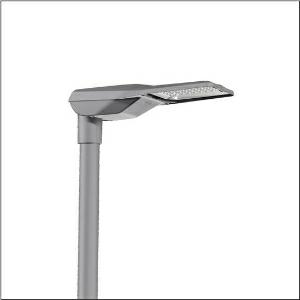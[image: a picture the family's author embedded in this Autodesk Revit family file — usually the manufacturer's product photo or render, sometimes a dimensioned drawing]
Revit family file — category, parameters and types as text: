
# Revit family: streetlight_sl_21_iq_mini___st1_5a_5xe2p31g08hb_126e
name_source: partatom
category: Lighting Fixtures
units: mm (PartAtom-declared; Revit-internal decimal feet)

## family parameters
Cut with Voids When Loaded = No
Host = Face
Light Source = No
Part Type = Normal
Room Calculation Point = No
Round Connector Dimension = Use Diameter
Shared = No

## types (1)
- --- (1 x LED, 9290 lm, 70.9 W, 3000K)
    Apparent Load = 71 VA
    CIE Flux Codes = 22 53 95 100 100
    Color Rendering = 70
    Color Temperature = 3000K
    Default Elevation = 1800 mm
    Description = Streetlight SL 21 iQ mini, mast luminaire, primary light control with lens, of PMMA, primary optical cover: cover, of toughened safety glass, transparent, light distribution: ST1.5a, light emission: direct distribution, primary light characteristic: asymmetric, installation type: post-top, side-entry, LED, High Power LED, rated luminous flux: 9.290lm, luminous efficacy: 131lm/W, light colour: 730, colour temperature: 3000K, control gear: iQ Street-Remote, control: Street-Remote, Auto-Match, Temp-Guard, Lumen-Switch, Night-Set, Smart-Wire, Light-Fading, Desk-Remote (wireless, voltage-free reading and setting of iQ features in the workshop via application-optimized NFC function/RFID function), optimised constant luminous flux control (CLO 2.0), pre-setting: linear dimming characteristic, mains connection: 220..240V, AC, 50/60Hz, start of lifetime: 71W, end of service life: 75W, reduction: 31W, luminaire housing, of diecast aluminium, powder-coated, Siteco® metallic grey (DB 702S), corrosivity category C5 mid according to DIN EN ISO 12944, please order mast flange separately, inclination adjustable: 0°, 5°, 10°, 15°, sealing non-destructively replaceable, multi-level sealing system, length: 628mm, width: 235mm, height: 110mm, mast flange for spigot size: 42mm (side-entry): 5XC10008XM4, 60/48mm (side-entry/post-top): 5XC10108XM2, 76/60mm (side-entry/post-top): 5XC10108XM1, mounting height: 4..8m, protection rating (complete): IP66, insulation class (complete): insulation class II (safety insulation), certification: CE, ENEC, ENEC+, VDE, impact resistance: IK10, permissible operating ambient temperature for outdoor applications: -40..+50°C, standard-compliant lighting for roads and squares, packaging unit: 1 piece

Light Distribution: ST1.5a
    Height = 110 mm
    Lamp = 1 x LED
    Lamp Light Flux = 9290 lm
    Lamp Power = 70.9 W
    Lamp count = 1
    Length = 625 mm
    Luminous efficacy = 131 lm/W
    Manufacturer = Siteco
    ModVariant = No
    Model = 5XE2P31G08HB
    Number of Poles = 1
    OnlyDefault = Yes
    Power Factor = 1
    Product Name = Streetlight SL 21 iQ mini | ST1.5a
    Product group = mast luminaire | pylon top
    ProductGroupID = 6100
    Protection Class = Protection class II
    Protection Degree = IP 66
    RLX_Detail_Level = 1
    RLX_Emergency_Light_Flux = 0 lm
    RLX_Emergency_Type = 0
    RLX_Emergency_Type_DB = No
    RlxData = <blob elided: 29897 chars, md5=f5cb2226>
    Socket = socket
    Standby Power = 0 W
    System Light Flux = 9290 lm
    System Power = 71 W
    Type Comments = factory setting: luminous flux: 100 % | dim-lin: 254 | 711 mA
    Type Image = l_1003519.jpg
    URL = http://relux.com
    VarID = @adj_178527
    Voltage = 0 V
    Weight = 0.00 kg
    Width = 234 mm

## geometry (parser evidence)
native form markers: Blend x4, Sweep x11
no freeform markers — native parametric forms only
